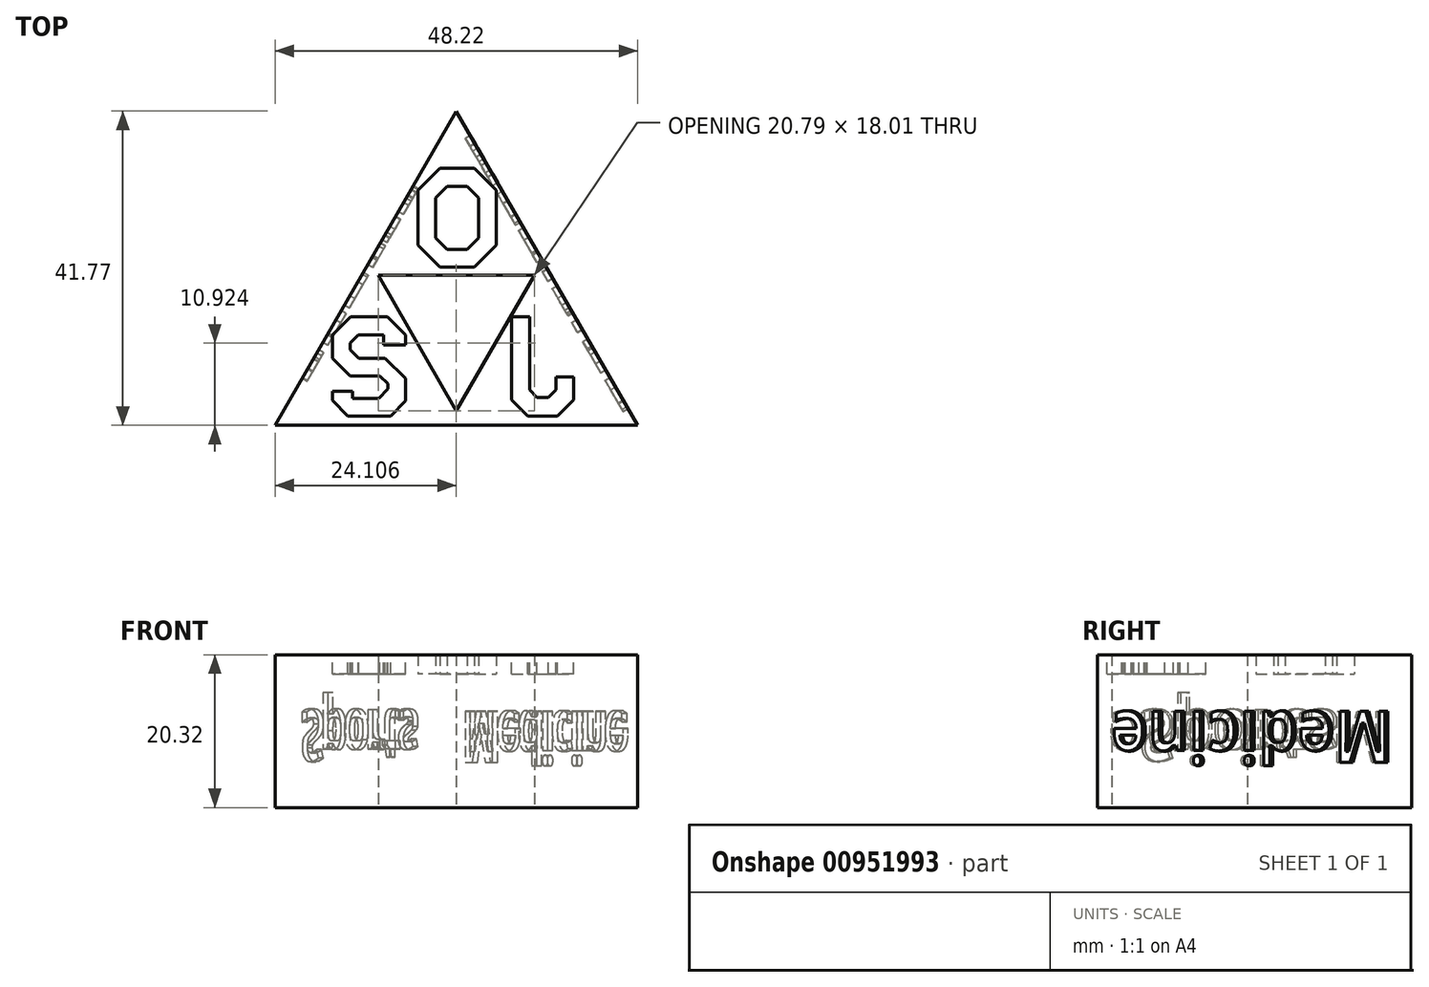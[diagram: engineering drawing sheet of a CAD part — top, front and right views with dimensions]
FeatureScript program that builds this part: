
annotation { "Feature Type Name" : "Feature", "Feature Type Description" : "" }
export const myFeature = defineFeature(function(context is Context, id is Id, definition is map)
    precondition{}
    {
        {
            var Q0;
            Q0=qCreatedBy(makeId("Top.planeOp"),FACE);
            var sketch = newSketch(context, id + "F0", { "sketchPlane" : qUnion([Q0])});
            skLineSegment(sketch, "E0", {"start": v(12.94, 23) * mm, "end": v(38.15, 23) * mm});
            skLineSegment(sketch, "E1", {"start": v(38.15, 23) * mm, "end": v(25.55, 44.84) * mm});
            skLineSegment(sketch, "E2", {"start": v(25.55, 44.84) * mm, "end": v(12.94, 23) * mm});
            skLineSegment(sketch, "E3", {"start": v(35.94, 23) * mm, "end": v(61.16, 23) * mm});
            skLineSegment(sketch, "E4", {"start": v(61.16, 23) * mm, "end": v(48.55, 44.85) * mm});
            skLineSegment(sketch, "E5", {"start": v(48.55, 44.85) * mm, "end": v(35.94, 23) * mm});
            skLineSegment(sketch, "E6", {"start": v(24.44, 42.93) * mm, "end": v(49.66, 42.93) * mm});
            skLineSegment(sketch, "E7", {"start": v(49.66, 42.93) * mm, "end": v(37.05, 64.77) * mm});
            skLineSegment(sketch, "E8", {"start": v(37.05, 64.77) * mm, "end": v(24.44, 42.93) * mm});
            skLineSegment(sketch, "E9", {"start": v(-28.9, 45.15) * mm, "end": v(-28.9, 27.37) * mm});
            skLineSegment(sketch, "E10", {"start": v(-28.9, 27.37) * mm, "end": v(-23.83, 22.3) * mm});
            skLineSegment(sketch, "E11", {"start": v(-23.83, 22.3) * mm, "end": v(-14.94, 22.3) * mm});
            skLineSegment(sketch, "E12", {"start": v(-14.94, 22.3) * mm, "end": v(-9.85, 27.37) * mm});
            skLineSegment(sketch, "E13", {"start": v(-9.85, 27.37) * mm, "end": v(-9.85, 45.15) * mm});
            skLineSegment(sketch, "E14", {"start": v(-9.85, 45.15) * mm, "end": v(-14.94, 50.24) * mm});
            skLineSegment(sketch, "E15", {"start": v(-14.94, 50.24) * mm, "end": v(-23.83, 50.24) * mm});
            skLineSegment(sketch, "E16", {"start": v(-23.83, 50.24) * mm, "end": v(-28.9, 45.15) * mm});
            skLineSegment(sketch, "E17.0", {"start": v(-11.68, 14.44) * mm, "end": v(-2, 24.12) * mm});
            skLineSegment(sketch, "E17.1", {"start": v(-27.08, 14.44) * mm, "end": v(-11.68, 14.44) * mm});
            skLineSegment(sketch, "E17.2", {"start": v(-2, 24.12) * mm, "end": v(-2, 48.4) * mm});
            skLineSegment(sketch, "E17.3", {"start": v(-36.76, 24.12) * mm, "end": v(-27.08, 14.44) * mm});
            skLineSegment(sketch, "E17.4", {"start": v(-2, 48.4) * mm, "end": v(-11.68, 58.09) * mm});
            skLineSegment(sketch, "E17.5", {"start": v(-11.68, 58.09) * mm, "end": v(-27.08, 58.09) * mm});
            skLineSegment(sketch, "E17.6", {"start": v(-27.08, 58.09) * mm, "end": v(-36.76, 48.4) * mm});
            skLineSegment(sketch, "E17.7", {"start": v(-36.76, 48.4) * mm, "end": v(-36.76, 24.12) * mm});
            skSolve(sketch);
        }
        {
            var Q0;
            Q0 = qSketchRegion(id + "F0", true);
            extrude(context, id + "F1", {"entities" : qUnion([Q0]), "depth" : 20.32 * mm, "offsetDistance" : 25.4 * mm});
        }
        {
            var Q0;
            Q0=makeQuery(id+"F1.opExtrude","SWEPT_BODY",BODY,{"disambiguationData":[OSD([sQuery(id+"F0.wireOp",EDGE,"E9"),sQuery(id+"F0.wireOp",EDGE,"E10"),sQuery(id+"F0.wireOp",EDGE,"E11"),sQuery(id+"F0.wireOp",EDGE,"E12"),sQuery(id+"F0.wireOp",EDGE,"E13"),sQuery(id+"F0.wireOp",EDGE,"E14"),sQuery(id+"F0.wireOp",EDGE,"E15"),sQuery(id+"F0.wireOp",EDGE,"E16"),sQuery(id+"F0.wireOp",EDGE,"E17.0"),sQuery(id+"F0.wireOp",EDGE,"E17.1"),sQuery(id+"F0.wireOp",EDGE,"E17.2"),sQuery(id+"F0.wireOp",EDGE,"E17.3"),sQuery(id+"F0.wireOp",EDGE,"E17.4"),sQuery(id+"F0.wireOp",EDGE,"E17.5"),sQuery(id+"F0.wireOp",EDGE,"E17.6"),sQuery(id+"F0.wireOp",EDGE,"E17.7")])]});
            var Q1;
            Q1=qCreatedBy(makeId("Origin.pointOp"),VERTEX);
            transform(context, id + "F2", {"entities" : qUnion([Q0]), "transformType" : TransformType.SCALE_UNIFORMLY, "scale" : 0.3, "scalePoint" : qUnion([Q1]), "makeCopy" : false});
        }
        {
            var Q0;
            Q0=makeQuery(id+"F1.opExtrude","SWEPT_BODY",BODY,{"disambiguationData":[OSD([sQuery(id+"F0.wireOp",EDGE,"E9"),sQuery(id+"F0.wireOp",EDGE,"E10"),sQuery(id+"F0.wireOp",EDGE,"E11"),sQuery(id+"F0.wireOp",EDGE,"E12"),sQuery(id+"F0.wireOp",EDGE,"E13"),sQuery(id+"F0.wireOp",EDGE,"E14"),sQuery(id+"F0.wireOp",EDGE,"E15"),sQuery(id+"F0.wireOp",EDGE,"E16"),sQuery(id+"F0.wireOp",EDGE,"E17.0"),sQuery(id+"F0.wireOp",EDGE,"E17.1"),sQuery(id+"F0.wireOp",EDGE,"E17.2"),sQuery(id+"F0.wireOp",EDGE,"E17.3"),sQuery(id+"F0.wireOp",EDGE,"E17.4"),sQuery(id+"F0.wireOp",EDGE,"E17.5"),sQuery(id+"F0.wireOp",EDGE,"E17.6"),sQuery(id+"F0.wireOp",EDGE,"E17.7")])]});
            transform(context, id + "F3", {"entities" : qUnion([Q0]), "transformType" : TransformType.TRANSLATION_3D, "dx" : 42.98 * mm, "dy" : 39.73 * mm, "dz" : 17.78 * mm, "makeCopy" : false});
        }
        {
            var Q0;
            Q0=makeQuery(id+"F1.opExtrude","SWEPT_BODY",BODY,{"disambiguationData":[OSD([sQuery(id+"F0.wireOp",EDGE,"E9"),sQuery(id+"F0.wireOp",EDGE,"E10"),sQuery(id+"F0.wireOp",EDGE,"E11"),sQuery(id+"F0.wireOp",EDGE,"E12"),sQuery(id+"F0.wireOp",EDGE,"E13"),sQuery(id+"F0.wireOp",EDGE,"E14"),sQuery(id+"F0.wireOp",EDGE,"E15"),sQuery(id+"F0.wireOp",EDGE,"E16"),sQuery(id+"F0.wireOp",EDGE,"E17.0"),sQuery(id+"F0.wireOp",EDGE,"E17.1"),sQuery(id+"F0.wireOp",EDGE,"E17.2"),sQuery(id+"F0.wireOp",EDGE,"E17.3"),sQuery(id+"F0.wireOp",EDGE,"E17.4"),sQuery(id+"F0.wireOp",EDGE,"E17.5"),sQuery(id+"F0.wireOp",EDGE,"E17.6"),sQuery(id+"F0.wireOp",EDGE,"E17.7")])]});
            var Q1;
            Q1=makeQuery(id+"F1.opExtrude","SWEPT_BODY",BODY,{"disambiguationData":[OSD([sQuery(id+"F0.wireOp",EDGE,"E0"),sQuery(id+"F0.wireOp",EDGE,"E1"),sQuery(id+"F0.wireOp",EDGE,"E2"),sQuery(id+"F0.wireOp",EDGE,"E3"),sQuery(id+"F0.wireOp",EDGE,"E4"),sQuery(id+"F0.wireOp",EDGE,"E5"),sQuery(id+"F0.wireOp",EDGE,"E6"),sQuery(id+"F0.wireOp",EDGE,"E7"),sQuery(id+"F0.wireOp",EDGE,"E8")])]});
            booleanBodies(context, id + "F4", {"operationType" : BooleanOperationType.SUBTRACTION, "tools" : qUnion([Q0]), "targets" : qUnion([Q1])});
        }
        {
            var Q0;
            Q0=makeQuery(id+"F1.opExtrude","SWEPT_FACE",FACE,{"disambiguationData":[OSD([sQuery(id+"F0.wireOp",EDGE,"E2"),sQuery(id+"F0.wireOp",EDGE,"E8")])]});
            var sketch = newSketch(context, id + "F5", { "sketchPlane" : qUnion([Q0])});
            skText(sketch, "E18", { "text": "Sports", "fontName": "OpenSans-Bold.ttf"});
            const initialGuessF5  = {"E18": [-0.03312, 0.013, -1, 0, 0.00686]};
            skSetInitialGuess(sketch, initialGuessF5);
            skSolve(sketch);
        }
        {
            var Q0;
            Q0 = qSketchRegion(id + "F5", true);
            extrude(context, id + "F6", {"entities" : qUnion([Q0]), "operationType" : NewBodyOperationType.REMOVE, "oppositeDirection" : true, "depth" : 0.76 * mm, "offsetDistance" : 25.4 * mm});
        }
        {
            var Q0;
            Q0=makeQuery(id+"F1.opExtrude","SWEPT_FACE",FACE,{"disambiguationData":[OSD([sQuery(id+"F0.wireOp",EDGE,"E4"),sQuery(id+"F0.wireOp",EDGE,"E7")])]});
            var sketch = newSketch(context, id + "F7", { "sketchPlane" : qUnion([Q0])});
            skText(sketch, "E19", { "text": "Medicine", "fontName": "OpenSans-Bold.ttf"});
            const initialGuessF7  = {"E19": [0.03473, 0.01279, -1, 0, 0.00686]};
            skSetInitialGuess(sketch, initialGuessF7);
            skSolve(sketch);
        }
        {
            var Q0;
            Q0 = qSketchRegion(id + "F7", true);
            extrude(context, id + "F8", {"entities" : qUnion([Q0]), "operationType" : NewBodyOperationType.REMOVE, "oppositeDirection" : true, "depth" : 0.76 * mm, "offsetDistance" : 25.4 * mm});
        }
        {
            var Q0;
            {var subQ0=sQuery(id+"F0.wireOp",EDGE,"E6");var subQ1=sQuery(id+"F0.wireOp",EDGE,"E5");var subQ2=sQuery(id+"F0.wireOp",EDGE,"E3");var subQ3=sQuery(id+"F0.wireOp",EDGE,"E0");var subQ4=sQuery(id+"F0.wireOp",EDGE,"E1");var subQ5=sQuery(id+"F0.wireOp",EDGE,"E8");var subQ6=sQuery(id+"F0.wireOp",EDGE,"E2");var subQ7=sQuery(id+"F0.wireOp",EDGE,"E7");var subQ8=sQuery(id+"F0.wireOp",EDGE,"E4");Q0=makeQuery(id+"F4.opBoolean","SPLIT",FACE,{"disambiguationData":[TD([makeQuery(id+"F1.opExtrude","SWEPT_FACE",FACE,{"disambiguationData":[OSD([subQ4])]})])],"derivedFrom":makeQuery(id+"F1.opExtrude","CAP_FACE",FACE,{"disambiguationData":[OSD([subQ3,subQ4,subQ6,subQ2,subQ8,subQ1,subQ0,subQ7,subQ5])],"isStart":false})});}
            var sketch = newSketch(context, id + "F9", { "sketchPlane" : qUnion([Q0])});
            skLineSegment(sketch, "E20.bottom", {"start": v(20.59, 37.42) * mm, "end": v(30.28, 37.42) * mm});
            skLineSegment(sketch, "E20.top", {"start": v(20.59, 24.25) * mm, "end": v(30.28, 24.25) * mm});
            skLineSegment(sketch, "E20.left", {"start": v(20.59, 37.42) * mm, "end": v(20.59, 24.25) * mm});
            skLineSegment(sketch, "E20.right", {"start": v(30.28, 37.42) * mm, "end": v(30.28, 24.25) * mm});
            skLineSegment(sketch, "E21", {"start": v(27.9, 37.42) * mm, "end": v(22.97, 37.42) * mm});
            skLineSegment(sketch, "E22", {"start": v(22.97, 37.42) * mm, "end": v(20.59, 35.03) * mm});
            skLineSegment(sketch, "E23", {"start": v(20.59, 35.03) * mm, "end": v(20.59, 31.94) * mm});
            skLineSegment(sketch, "E24", {"start": v(20.59, 31.94) * mm, "end": v(22.94, 29.58) * mm});
            skLineSegment(sketch, "E25", {"start": v(22.94, 29.58) * mm, "end": v(26.86, 29.58) * mm});
            skLineSegment(sketch, "E26", {"start": v(26.86, 29.58) * mm, "end": v(27.93, 28.52) * mm});
            skLineSegment(sketch, "E27", {"start": v(27.93, 28.52) * mm, "end": v(27.93, 27.82) * mm});
            skLineSegment(sketch, "E28", {"start": v(27.93, 27.82) * mm, "end": v(26.71, 26.6) * mm});
            skLineSegment(sketch, "E29", {"start": v(26.71, 26.6) * mm, "end": v(23.26, 26.6) * mm});
            skLineSegment(sketch, "E30", {"start": v(23.26, 26.6) * mm, "end": v(23.26, 27.5) * mm});
            skLineSegment(sketch, "E31", {"start": v(23.26, 27.5) * mm, "end": v(20.59, 27.5) * mm});
            skLineSegment(sketch, "E32", {"start": v(20.59, 27.5) * mm, "end": v(20.59, 26.3) * mm});
            skLineSegment(sketch, "E33", {"start": v(20.59, 26.3) * mm, "end": v(22.64, 24.25) * mm});
            skLineSegment(sketch, "E34", {"start": v(22.64, 24.25) * mm, "end": v(28.3, 24.25) * mm});
            skLineSegment(sketch, "E35", {"start": v(28.3, 24.25) * mm, "end": v(30.28, 26.23) * mm});
            skLineSegment(sketch, "E36", {"start": v(30.28, 26.23) * mm, "end": v(30.28, 29.22) * mm});
            skLineSegment(sketch, "E37", {"start": v(30.28, 29.22) * mm, "end": v(27.57, 31.93) * mm});
            skLineSegment(sketch, "E38", {"start": v(27.57, 31.93) * mm, "end": v(24.08, 31.93) * mm});
            skLineSegment(sketch, "E39", {"start": v(24.08, 31.93) * mm, "end": v(22.95, 33.07) * mm});
            skLineSegment(sketch, "E40", {"start": v(22.95, 33.07) * mm, "end": v(22.95, 33.95) * mm});
            skLineSegment(sketch, "E41", {"start": v(22.95, 33.95) * mm, "end": v(24.02, 35.02) * mm});
            skLineSegment(sketch, "E42", {"start": v(24.02, 35.02) * mm, "end": v(27.37, 35.02) * mm});
            skLineSegment(sketch, "E43", {"start": v(27.37, 35.02) * mm, "end": v(27.37, 33.7) * mm});
            skLineSegment(sketch, "E44", {"start": v(27.37, 33.7) * mm, "end": v(30.28, 33.7) * mm});
            skLineSegment(sketch, "E45", {"start": v(30.28, 33.7) * mm, "end": v(30.28, 35.03) * mm});
            skLineSegment(sketch, "E46", {"start": v(30.28, 35.03) * mm, "end": v(27.9, 37.42) * mm});
            skLineSegment(sketch, "E47", {"start": v(24.58, 26.7) * mm, "end": v(24.58, 24.34) * mm});
            skLineSegment(sketch, "E48", {"start": v(24.58, 31.94) * mm, "end": v(24.58, 29.58) * mm});
            skLineSegment(sketch, "E49", {"start": v(24.58, 37.47) * mm, "end": v(24.58, 35.12) * mm});
            skLineSegment(sketch, "E50", {"start": v(22.94, 33.89) * mm, "end": v(20.59, 33.89) * mm});
            skLineSegment(sketch, "E51", {"start": v(30.28, 28.16) * mm, "end": v(27.93, 28.16) * mm});
            skLineSegment(sketch, "E52.bottom", {"start": v(44.41, 37.42) * mm, "end": v(52.65, 37.42) * mm});
            skLineSegment(sketch, "E52.top", {"start": v(44.41, 24.25) * mm, "end": v(52.65, 24.25) * mm});
            skLineSegment(sketch, "E52.left", {"start": v(44.41, 37.42) * mm, "end": v(44.41, 24.25) * mm});
            skLineSegment(sketch, "E52.right", {"start": v(52.65, 37.42) * mm, "end": v(52.65, 24.25) * mm});
            skLineSegment(sketch, "E53", {"start": v(50.31, 27.72) * mm, "end": v(49.3, 26.7) * mm});
            skLineSegment(sketch, "E54", {"start": v(46.78, 27.71) * mm, "end": v(46.78, 37.42) * mm});
            skLineSegment(sketch, "E55", {"start": v(46.78, 37.42) * mm, "end": v(44.41, 37.42) * mm});
            skLineSegment(sketch, "E56", {"start": v(44.41, 37.42) * mm, "end": v(44.41, 26.38) * mm});
            skLineSegment(sketch, "E57", {"start": v(44.41, 26.38) * mm, "end": v(46.54, 24.25) * mm});
            skLineSegment(sketch, "E58", {"start": v(46.54, 24.25) * mm, "end": v(50.52, 24.25) * mm});
            skLineSegment(sketch, "E59", {"start": v(50.52, 24.25) * mm, "end": v(52.65, 26.38) * mm});
            skLineSegment(sketch, "E60", {"start": v(52.65, 26.38) * mm, "end": v(52.65, 37.42) * mm});
            skLineSegment(sketch, "E61", {"start": v(47.64, 26.7) * mm, "end": v(47.64, 24.34) * mm});
            skLineSegment(sketch, "E62", {"start": v(46.76, 33.89) * mm, "end": v(44.41, 33.89) * mm});
            skLineSegment(sketch, "E63", {"start": v(52.66, 29.44) * mm, "end": v(50.3, 29.44) * mm});
            skLineSegment(sketch, "E64", {"start": v(46.78, 27.71) * mm, "end": v(47.79, 26.7) * mm});
            skLineSegment(sketch, "E65", {"start": v(47.79, 26.7) * mm, "end": v(49.3, 26.7) * mm});
            skLineSegment(sketch, "E66", {"start": v(50.31, 27.72) * mm, "end": v(50.31, 37.42) * mm});
            skLineSegment(sketch, "E67", {"start": v(50.31, 37.42) * mm, "end": v(52.65, 37.42) * mm});
            skSolve(sketch);
        }
        {
            var Q0;
            {var subQ5=sQuery(id+"F9.wireOp",EDGE,"E26");Q0=makeQuery(id+"F9.imprint","IMPRINT",FACE,{"disambiguationData":[TD([[makeQuery(id+"F9.imprint","IMPRINT",EDGE,{"derivedFrom":subQ5}),1.0]])]});}
            var Q1;
            {var subQ2=sQuery(id+"F9.wireOp",EDGE,"E28");Q1=makeQuery(id+"F9.imprint","IMPRINT",FACE,{"disambiguationData":[TD([[makeQuery(id+"F9.imprint","IMPRINT",EDGE,{"derivedFrom":subQ2}),1.0]])]});}
            var Q2;
            {var subQ5=sQuery(id+"F9.wireOp",EDGE,"E22");Q2=makeQuery(id+"F9.imprint","IMPRINT",FACE,{"disambiguationData":[TD([[makeQuery(id+"F9.imprint","IMPRINT",EDGE,{"derivedFrom":subQ5}),1.0]])]});}
            var Q3;
            {var subQ9=sQuery(id+"F9.wireOp",EDGE,"E53");Q3=makeQuery(id+"F9.imprint","IMPRINT",FACE,{"disambiguationData":[TD([[makeQuery(id+"F9.imprint","IMPRINT",EDGE,{"derivedFrom":subQ9}),1.0]])]});}
            var Q4;
            {var subQ0=sQuery(id+"F9.wireOp",EDGE,"E67");Q4=makeQuery(id+"F9.imprint","IMPRINT",FACE,{"disambiguationData":[TD([[makeQuery(id+"F9.imprint","IMPRINT",EDGE,{"derivedFrom":subQ0}),-1.0]])]});}
            extrude(context, id + "F10", {"entities" : qUnion([Q0, Q1, Q2, Q3, Q4]), "operationType" : NewBodyOperationType.REMOVE, "oppositeDirection" : true, "depth" : 2.54 * mm, "offsetDistance" : 25.4 * mm});
        }
    });
